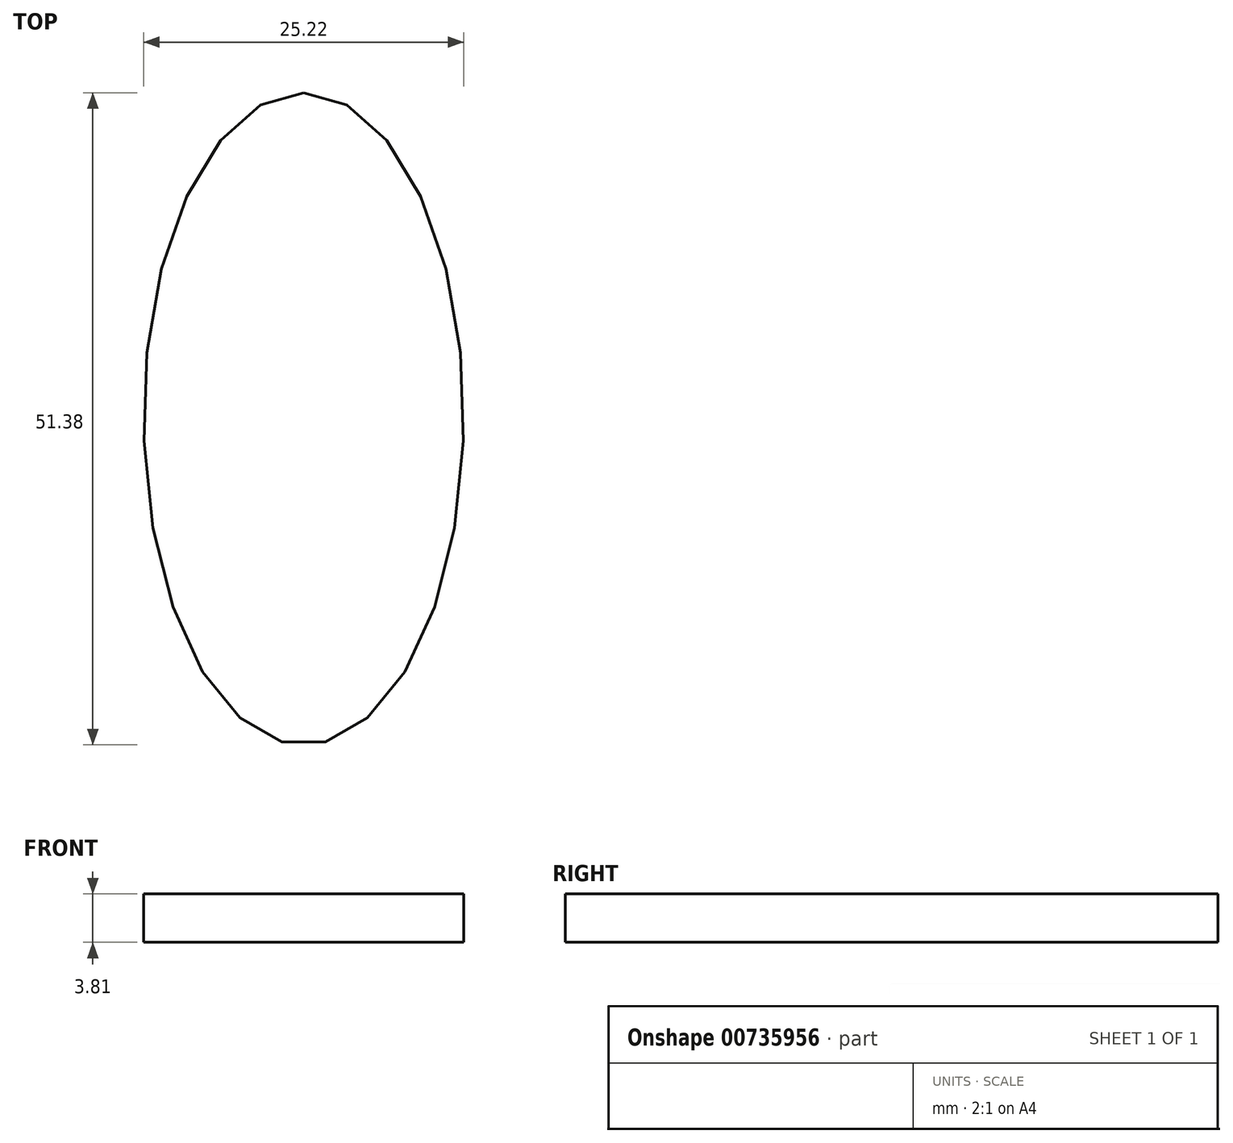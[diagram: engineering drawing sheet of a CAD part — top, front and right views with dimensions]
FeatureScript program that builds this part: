
annotation { "Feature Type Name" : "Feature", "Feature Type Description" : "" }
export const myFeature = defineFeature(function(context is Context, id is Id, definition is map)
    precondition{}
    {
        {
            var Q0;
            Q0=qCreatedBy(makeId("Top.planeOp"),FACE);
            var sketch = newSketch(context, id + "F0", { "sketchPlane" : qUnion([Q0])});
            skEllipse(sketch, "E0", {"center": v(0, 0) * mm, "majorRadius": 25.7 * mm, "minorRadius": 12.61 * mm, "majorAxis": v(0, 1)});
            skSolve(sketch);
        }
        {
            var Q0;
            Q0=makeQuery(id+"F0.imprint","IMPRINT",FACE,{"disambiguationData":[TD([[makeQuery(id+"F0.imprint","IMPRINT",EDGE,{"derivedFrom":sQuery(id+"F0.wireOp",EDGE,"E0")}),1.0]])]});
            extrude(context, id + "F1", {"entities" : qUnion([Q0]), "depth" : 3.8 * mm, "offsetDistance" : 25.4 * mm});
        }
    });
